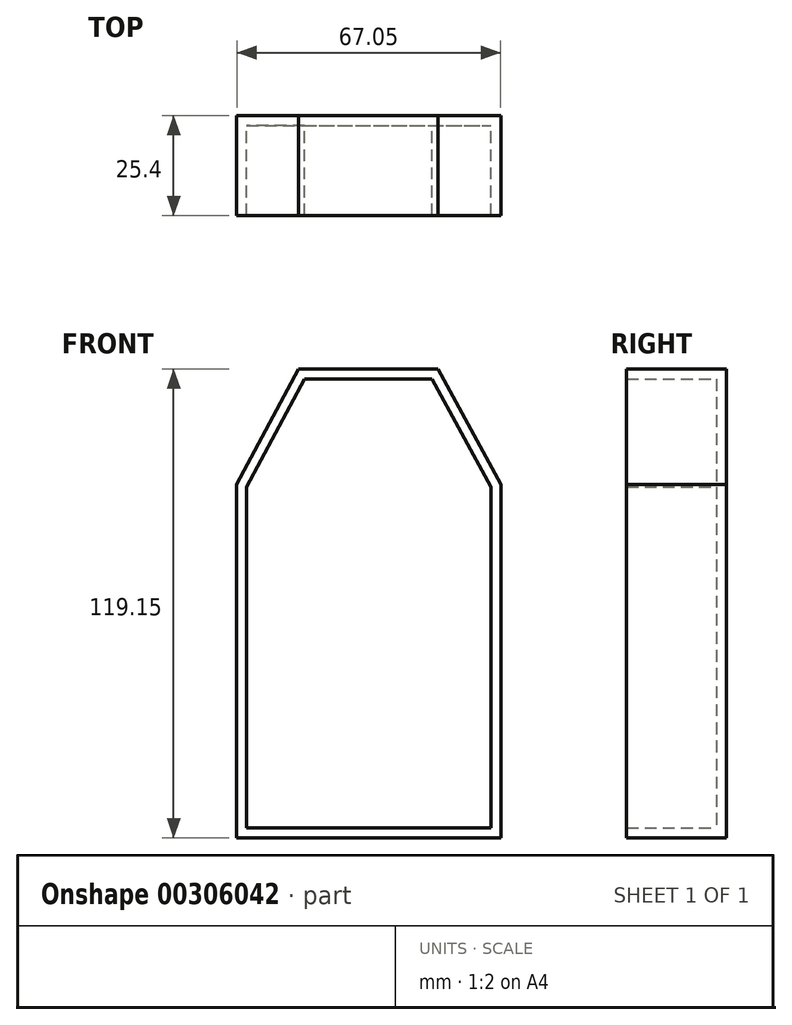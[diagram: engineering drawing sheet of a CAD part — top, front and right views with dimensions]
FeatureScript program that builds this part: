
annotation { "Feature Type Name" : "Feature", "Feature Type Description" : "" }
export const myFeature = defineFeature(function(context is Context, id is Id, definition is map)
    precondition{}
    {
        {
            var Q0;
            Q0=qCreatedBy(makeId("Front.planeOp"),FACE);
            var sketch = newSketch(context, id + "F0", { "sketchPlane" : qUnion([Q0])});
            skLineSegment(sketch, "E0", {"start": v(-28.32, 46.05) * mm, "end": v(7.04, 46.05) * mm});
            skLineSegment(sketch, "E1", {"start": v(-28.32, 46.05) * mm, "end": v(-44.03, 16.7) * mm});
            skLineSegment(sketch, "E2", {"start": v(7.04, 46.05) * mm, "end": v(23.02, 16.7) * mm});
            skLineSegment(sketch, "E3", {"start": v(-44.03, 16.7) * mm, "end": v(-44.03, -73.1) * mm});
            skLineSegment(sketch, "E4", {"start": v(23.02, 16.7) * mm, "end": v(23.02, -73.1) * mm});
            skLineSegment(sketch, "E5", {"start": v(-44.03, -73.1) * mm, "end": v(23.02, -73.1) * mm});
            skSolve(sketch);
        }
        {
            var Q0;
            Q0 = qSketchRegion(id + "F0", true);
            extrude(context, id + "F1", {"entities" : qUnion([Q0]), "depth" : 25.4 * mm});
        }
        {
            var Q0;
            Q0=makeQuery(id+"F1.opExtrude","CAP_FACE",FACE,{"disambiguationData":[OSD([sQuery(id+"F0.wireOp",EDGE,"E0"),sQuery(id+"F0.wireOp",EDGE,"E1"),sQuery(id+"F0.wireOp",EDGE,"E2"),sQuery(id+"F0.wireOp",EDGE,"E3"),sQuery(id+"F0.wireOp",EDGE,"E4"),sQuery(id+"F0.wireOp",EDGE,"E5")])],"isStart":false});
            shell(context, id + "F2", {"entities" : qUnion([Q0]), "thickness" : 2.54 * mm});
        }
    });
